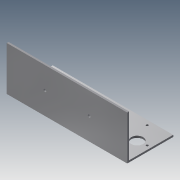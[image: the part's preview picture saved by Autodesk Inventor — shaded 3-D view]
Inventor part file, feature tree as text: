
AUTODESK INVENTOR PART (.ipt)
format: ipt  version: 2013 (Build 170138000, 138)  size: 162,816 bytes
history: native  units: mm
features: sketch x9, extrude x6, hole x3
ambient origin geometry x8: Origin, YZ Plane, XZ Plane, XY Plane, X Axis, Y Axis, Z Axis, Center Point
bodies: Solid1 (feature_tree)
feature tree (18):
  extrude  "Extrusion1"  Depth=7.0mm
  hole  "Hole1"  [1 undecoded]
  hole  "Hole2"  [1 undecoded]
  hole  "Hole4"  [1 undecoded]
  extrude  "Extrusion3"  Depth=2.4mm
  extrude  "Extrusion4"  Depth=7.0mm
  extrude  "Extrusion6"  Depth=31.0mm
  extrude  "Extrusion7"  Depth=25.0mm
  extrude  "Extrusion8"  TaperAngle=180.0deg  [1 undecoded]
  sketch  "Sketch1"  dims[d11=131.0mm d12=0.0mm d17=7.0mm]
  sketch  "Sketch2"  dims[d18=7.0mm]
  sketch  "Sketch3"  dims[d19=7.0mm d20=6.0mm d21=4.0mm d22=2.0mm d23=90.0deg d24=2.0mm d25=0.0mm d26=51.3mm]
  sketch  "Sketch5"  dims[d27=51.3mm d28=19.0mm]
  sketch  "Sketch7"  dims[d29=3.5mm d30=3.5mm]
  sketch  "Sketch8"  dims[d31=3.5mm d32=6.0mm d33=4.0mm d34=2.0mm d35=90.0deg d36=2.0mm d37=0.0mm d62=2.4mm]
  sketch  "Sketch9"  dims[d63=2.4mm]
  sketch  "Sketch11"  dims[d64=3.0mm d65=2.0mm d66=4.0mm d67=2.0mm d68=90.0deg d69=2.0mm d70=0.0mm d89=7.0mm]
  sketch  "Sketch12"  dims[d90=2.0mm d91=0.0mm d96=31.0mm d97=25.0mm d98=180.0deg d99=50.0mm d100=2.4mm d101=2.4mm d104=2.4mm d105=2.4mm d106=2.4mm d107=2.4mm d108=2.0mm d109=0.0mm d112=2.0mm d113=0.0mm d114=2.0mm d115=0.0mm d116=13.0mm d117=13.0mm d118=2.0mm d119=0.0mm]
note: 4 required parameter values undecoded (feature->parameter linkage not recoverable at this tier; creation-order binding heuristic only, values carry confidence <= 0.55)
